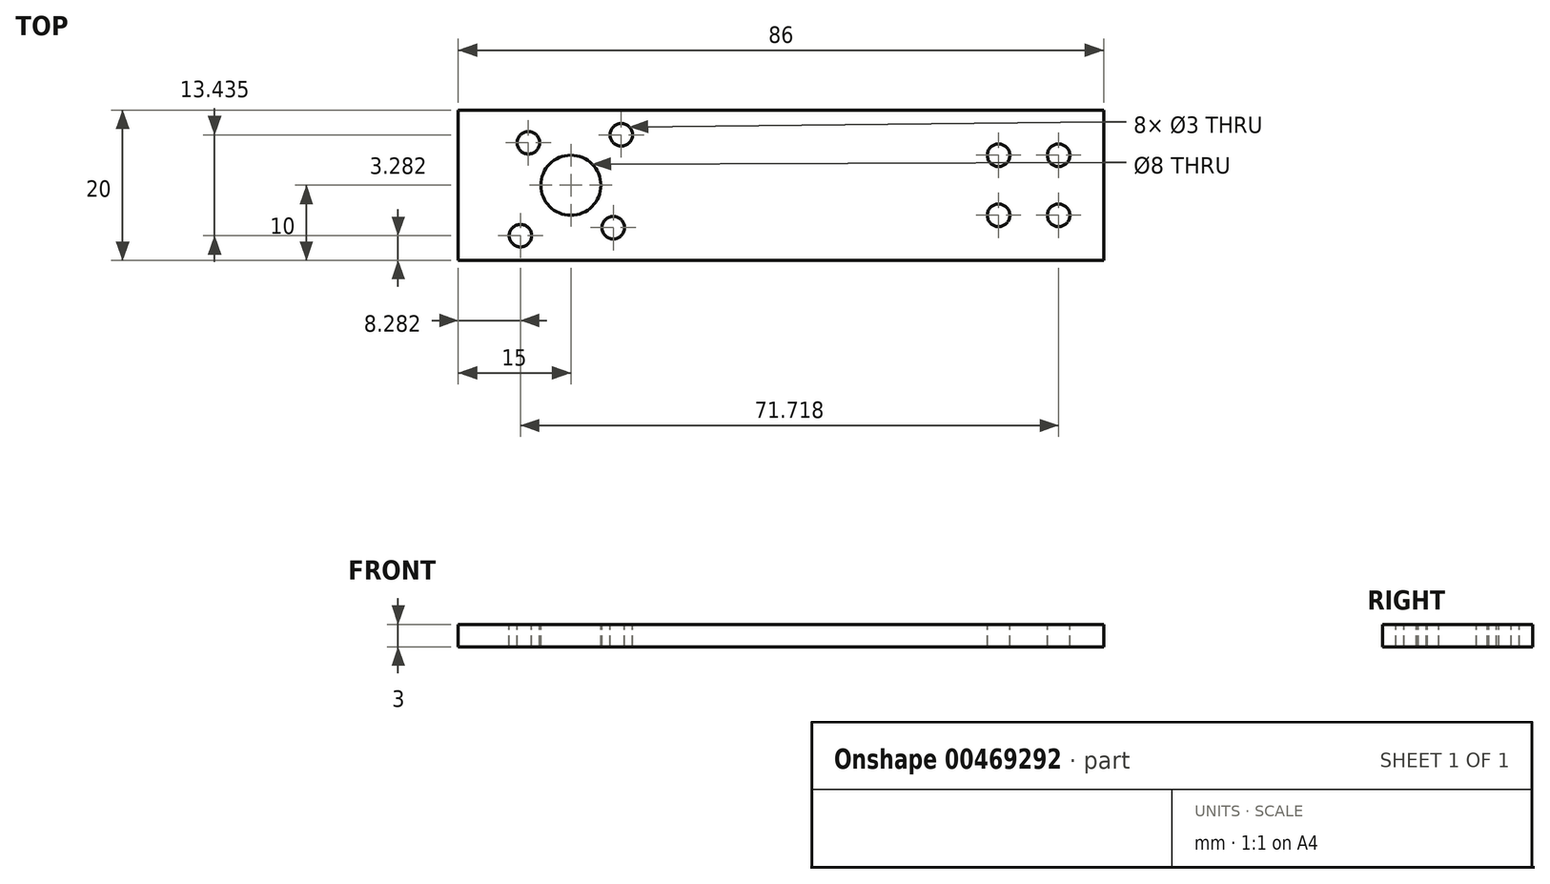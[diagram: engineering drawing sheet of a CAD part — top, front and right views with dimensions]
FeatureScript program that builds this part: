
annotation { "Feature Type Name" : "Feature", "Feature Type Description" : "" }
export const myFeature = defineFeature(function(context is Context, id is Id, definition is map)
    precondition{}
    {
        {
            var Q0;
            Q0=qCreatedBy(makeId("Top.planeOp"),FACE);
            var sketch = newSketch(context, id + "F0", { "sketchPlane" : qUnion([Q0])});
            skLineSegment(sketch, "E0.bottom", {"start": v(-43, 10) * mm, "end": v(43, 10) * mm});
            skLineSegment(sketch, "E0.top", {"start": v(-43, -10) * mm, "end": v(43, -10) * mm});
            skLineSegment(sketch, "E0.left", {"start": v(-43, 10) * mm, "end": v(-43, -10) * mm});
            skLineSegment(sketch, "E0.right", {"start": v(43, 10) * mm, "end": v(43, -10) * mm});
            skPoint(sketch, "E0.middle", {"position": v(0, 0) * mm});
            skSolve(sketch);
        }
        {
            var Q0;
            Q0=makeQuery(id+"F0.imprint","IMPRINT",FACE,{"disambiguationData":[TD([[makeQuery(id+"F0.imprint","IMPRINT",EDGE,{"derivedFrom":sQuery(id+"F0.wireOp",EDGE,"E0.bottom")}),-1.0]])]});
            extrude(context, id + "F1", {"entities" : qUnion([Q0]), "depth" : 3 * mm, "offsetDistance" : 25 * mm});
        }
        {
            var Q0;
            Q0=makeQuery(id+"F1.opExtrude","CAP_FACE",FACE,{"disambiguationData":[OSD([sQuery(id+"F0.wireOp",EDGE,"E0.bottom"),sQuery(id+"F0.wireOp",EDGE,"E0.top"),sQuery(id+"F0.wireOp",EDGE,"E0.left"),sQuery(id+"F0.wireOp",EDGE,"E0.right")])],"isStart":false});
            var sketch = newSketch(context, id + "F2", { "sketchPlane" : qUnion([Q0])});
            skPoint(sketch, "E1", {"position": v(37, -4) * mm});
            skPoint(sketch, "E2", {"position": v(37, 4) * mm});
            skPoint(sketch, "E3", {"position": v(29, 4) * mm});
            skPoint(sketch, "E4", {"position": v(29, -4) * mm});
            skPoint(sketch, "E5", {"position": v(-28, 0) * mm});
            skLineSegment(sketch, "E6", {"start": v(-14.76, 13.24) * mm, "end": v(-41.24, -13.24) * mm, "construction": true});
            skLineSegment(sketch, "E7", {"start": v(-39.7, 11.7) * mm, "end": v(-16.3, -11.7) * mm, "construction": true});
            skPoint(sketch, "E8", {"position": v(-21.28, 6.72) * mm});
            skPoint(sketch, "E9", {"position": v(-22.34, -5.66) * mm});
            skPoint(sketch, "E10", {"position": v(-34.72, -6.72) * mm});
            skPoint(sketch, "E11", {"position": v(-33.66, 5.66) * mm});
            skCircle(sketch, "E12", {"center": v(-28, 0) * mm, "radius": 8 * mm, "construction": true});
            skCircle(sketch, "E13", {"center": v(-28, 0) * mm, "radius": 9.5 * mm, "construction": true});
            skSolve(sketch);
        }
        {
            var Q0;
            Q0=sQuery(id+"F2.wireOp",VERTEX,"E2");
            var Q1;
            Q1=sQuery(id+"F2.wireOp",VERTEX,"E1");
            var Q2;
            Q2=sQuery(id+"F2.wireOp",VERTEX,"E4");
            var Q3;
            Q3=sQuery(id+"F2.wireOp",VERTEX,"E3");
            var Q4;
            Q4=makeQuery(id+"F1.opExtrude","SWEPT_BODY",BODY,{"disambiguationData":[OSD([sQuery(id+"F0.wireOp",EDGE,"E0.bottom"),sQuery(id+"F0.wireOp",EDGE,"E0.top"),sQuery(id+"F0.wireOp",EDGE,"E0.left"),sQuery(id+"F0.wireOp",EDGE,"E0.right")])]});
            hole(context, id + "F3", {"style" : HoleStyle.SIMPLE, "endStyle" : HoleEndStyle.THROUGH, "holeDiameter" : 3 * mm, "isTappedThrough" : true, "tappedDepth" : 12 * mm, "tapClearance" : 3, "locations" : qUnion([Q0, Q1, Q2, Q3]), "scope" : qUnion([Q4]), "majorDiameter" : 5 * mm});
        }
        {
            var Q0;
            Q0=sQuery(id+"F2.wireOp",VERTEX,"E5");
            var Q1;
            Q1=makeQuery(id+"F1.opExtrude","SWEPT_BODY",BODY,{"disambiguationData":[OSD([sQuery(id+"F0.wireOp",EDGE,"E0.bottom"),sQuery(id+"F0.wireOp",EDGE,"E0.top"),sQuery(id+"F0.wireOp",EDGE,"E0.left"),sQuery(id+"F0.wireOp",EDGE,"E0.right")])]});
            hole(context, id + "F4", {"style" : HoleStyle.SIMPLE, "endStyle" : HoleEndStyle.THROUGH, "holeDiameter" : 8 * mm, "majorDiameter" : 5 * mm, "isTappedThrough" : true, "tappedDepth" : 12 * mm, "tapClearance" : 3, "locations" : qUnion([Q0]), "scope" : qUnion([Q1])});
        }
        {
            var Q0;
            Q0=sQuery(id+"F2.wireOp",VERTEX,"E10");
            var Q1;
            Q1=sQuery(id+"F2.wireOp",VERTEX,"E11");
            var Q2;
            Q2=sQuery(id+"F2.wireOp",VERTEX,"E8");
            var Q3;
            Q3=sQuery(id+"F2.wireOp",VERTEX,"E9");
            var Q4;
            Q4=makeQuery(id+"F1.opExtrude","SWEPT_BODY",BODY,{"disambiguationData":[OSD([sQuery(id+"F0.wireOp",EDGE,"E0.bottom"),sQuery(id+"F0.wireOp",EDGE,"E0.top"),sQuery(id+"F0.wireOp",EDGE,"E0.left"),sQuery(id+"F0.wireOp",EDGE,"E0.right")])]});
            hole(context, id + "F5", {"style" : HoleStyle.SIMPLE, "endStyle" : HoleEndStyle.THROUGH, "holeDiameter" : 3 * mm, "majorDiameter" : 5 * mm, "isTappedThrough" : true, "tappedDepth" : 12 * mm, "tapClearance" : 3, "locations" : qUnion([Q0, Q1, Q2, Q3]), "scope" : qUnion([Q4])});
        }
    });
